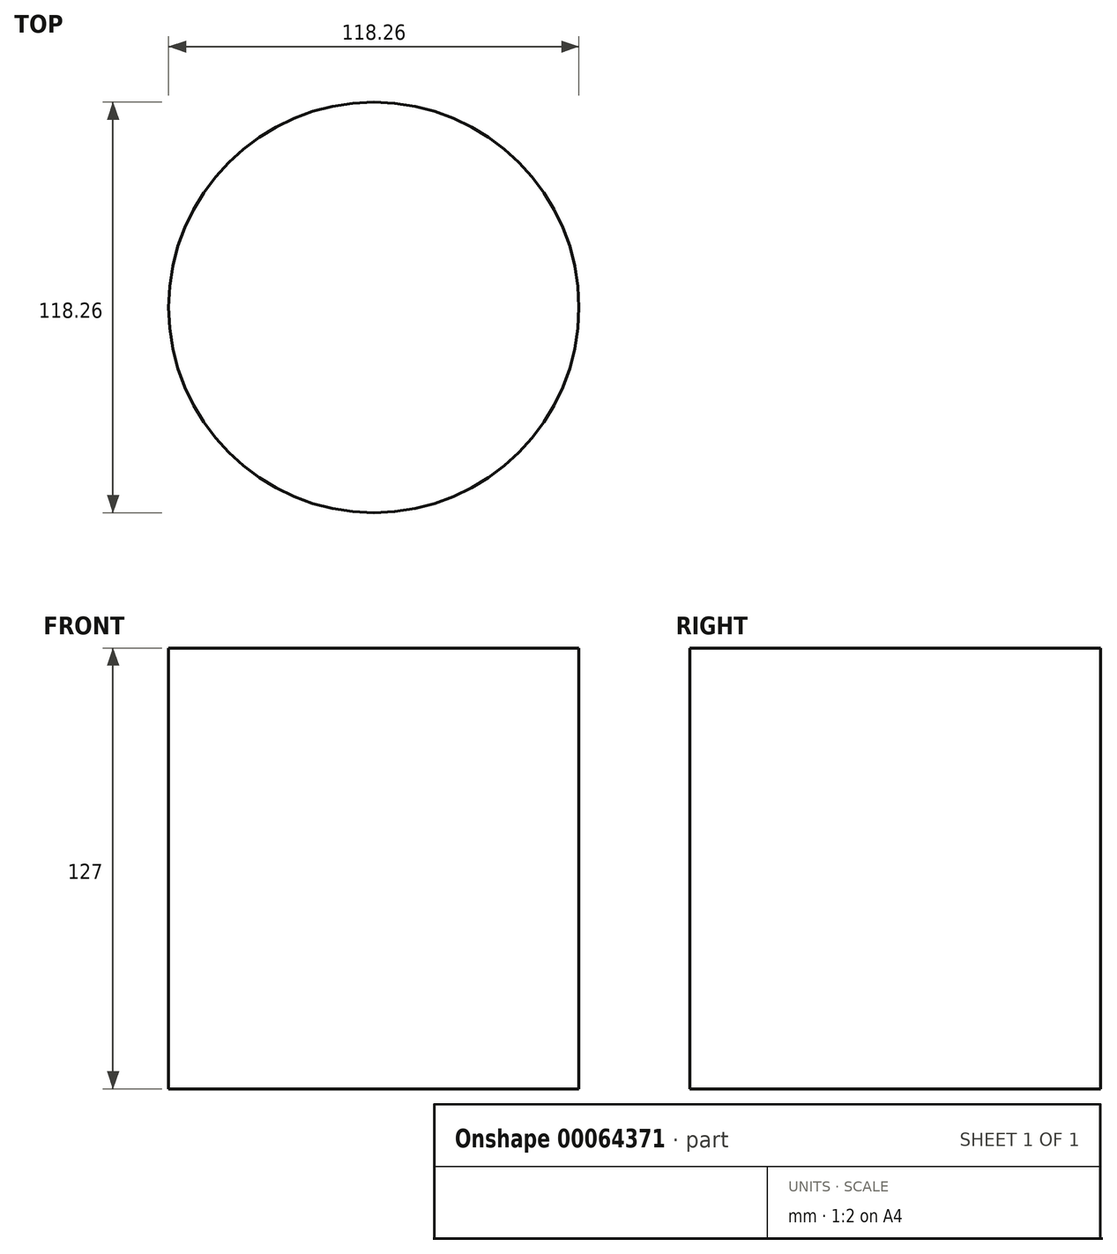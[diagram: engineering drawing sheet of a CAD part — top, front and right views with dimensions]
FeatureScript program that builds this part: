
annotation { "Feature Type Name" : "Feature", "Feature Type Description" : "" }
export const myFeature = defineFeature(function(context is Context, id is Id, definition is map)
    precondition{}
    {
        {
            var Q0;
            Q0=qCreatedBy(makeId("Top.planeOp"),FACE);
            var sketch = newSketch(context, id + "F0", { "sketchPlane" : qUnion([Q0])});
            skCircle(sketch, "E0", {"center": v(0, 0) * mm, "radius": 59.13 * mm});
            skSolve(sketch);
        }
        {
            var Q0;
            Q0=sQuery(id+"F0.wireOp",EDGE,"E0");
            extrude(context, id + "F1", {"bodyType" : ToolBodyType.SURFACE, "surfaceEntities" : qUnion([Q0]), "depth" : 127 * mm});
        }
    });
